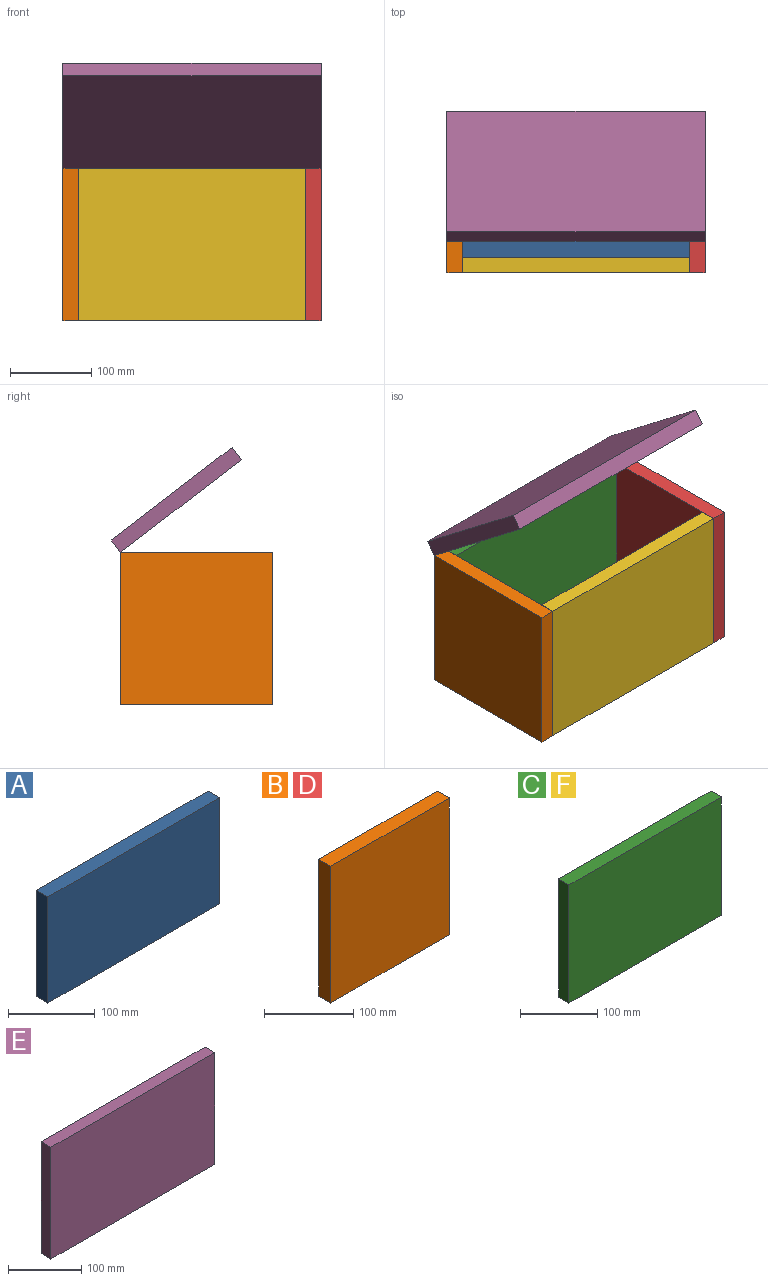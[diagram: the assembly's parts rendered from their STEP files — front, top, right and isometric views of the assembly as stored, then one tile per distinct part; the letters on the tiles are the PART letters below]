
ASSEMBLY  parts=6 mates=5
PART A: 6 faces, bbox 279.4x19.1x149.2 mm
  f0: plane 279.4x19.05mm, normal (0,0,1), area 5322.6mm2, adj f1,f3,f4,f5
  f1: plane 149.23x19.05mm, normal (-1,0,0), area 2842.7mm2, adj f0,f2,f4,f5
  f2: plane 279.4x19.05mm, normal (0,0,-1), area 5322.6mm2, adj f1,f3,f4,f5
  f3: plane 149.23x19.05mm, normal (1,0,0), area 2842.7mm2, adj f0,f2,f4,f5
  f4: plane 279.4x149.23mm, normal (0,-1,0), area 41693.5mm2, adj f0,f1,f2,f3
  f5: plane 279.4x149.23mm, normal (0,1,0), area 41693.5mm2, adj f0,f1,f2,f3
PART B: 6 faces, bbox 187.3x19.1x187.3 mm
  f0: plane 187.33x19.05mm, normal (0,0,1), area 3568.5mm2, adj f1,f3,f4,f5
  f1: plane 187.33x19.05mm, normal (-1,0,0), area 3568.5mm2, adj f0,f2,f4,f5
  f2: plane 187.33x19.05mm, normal (0,0,-1), area 3568.5mm2, adj f1,f3,f4,f5
  f3: plane 187.33x19.05mm, normal (1,0,0), area 3568.5mm2, adj f0,f2,f4,f5
  f4: plane 187.33x187.33mm, normal (0,-1,0), area 35090.7mm2, adj f0,f1,f2,f3
  f5: plane 187.33x187.33mm, normal (0,1,0), area 35090.7mm2, adj f0,f1,f2,f3
PART C: 6 faces, bbox 279.4x19.1x187.3 mm
  f0: plane 187.33x19.05mm, normal (-1,0,0), area 3568.5mm2, adj f1,f3,f4,f5
  f1: plane 279.4x19.05mm, normal (0,0,-1), area 5322.6mm2, adj f0,f2,f4,f5
  f2: plane 187.33x19.05mm, normal (1,0,0), area 3568.5mm2, adj f1,f3,f4,f5
  f3: plane 279.4x19.05mm, normal (0,0,1), area 5322.6mm2, adj f0,f2,f4,f5
  f4: plane 279.4x187.33mm, normal (0,-1,0), area 52338.6mm2, adj f0,f1,f2,f3
  f5: plane 279.4x187.33mm, normal (0,1,0), area 52338.6mm2, adj f0,f1,f2,f3
PART D: same geometry as B
PART E: 6 faces, bbox 317.5x19.1x187.3 mm
  f0: plane 317.5x19.05mm, normal (0,0,1), area 6048.4mm2, adj f1,f3,f4,f5
  f1: plane 187.33x19.05mm, normal (-1,0,0), area 3568.5mm2, adj f0,f2,f4,f5
  f2: plane 317.5x19.05mm, normal (0,0,-1), area 6048.4mm2, adj f1,f3,f4,f5
  f3: plane 187.33x19.05mm, normal (1,0,0), area 3568.5mm2, adj f0,f2,f4,f5
  f4: plane 317.5x187.33mm, normal (0,-1,0), area 59475.7mm2, adj f0,f1,f2,f3
  f5: plane 317.5x187.33mm, normal (0,1,0), area 59475.7mm2, adj f0,f1,f2,f3
PART F: same geometry as C
PLACE A rot(axis=(-1,0,0),90deg) t=(139.7,82.16,-93.66)mm
PLACE B rot(axis=(0,0,1),90deg) t=(-158.75,-130.01,60.96)mm
PLACE C rot(axis=(0.19,0.98,0),0deg) t=(-139.7,0,-93.66)mm
PLACE D rot(axis=(0,0,1),90deg) t=(139.7,-130.01,60.96)mm
PLACE E rot(axis=(1,0,0),52.6deg) t=(-3.5,52.94,77.12)mm
PLACE F rot(axis=(-0.76,-0.6,-0.25),0deg) t=(-139.7,-168.28,-93.66)mm
MATE fastened C.f0 <-> B.f4  axis (-1,0,0) through (-139.7,0,0)mm
MATE fastened A.f1 <-> B.f4  axis (-1,0,0) through (-139.7,-93.66,-93.66)mm
MATE fastened D.f5 <-> F.f2  axis (-1,0,0) through (139.7,-187.33,0)mm
MATE fastened B.f4 <-> F.f0  axis (1,0,0) through (-139.7,-187.33,0)mm
MATE revolute D.f4 <-> E.f3  axis (1,0,0) through (158.75,0,93.66)mm
